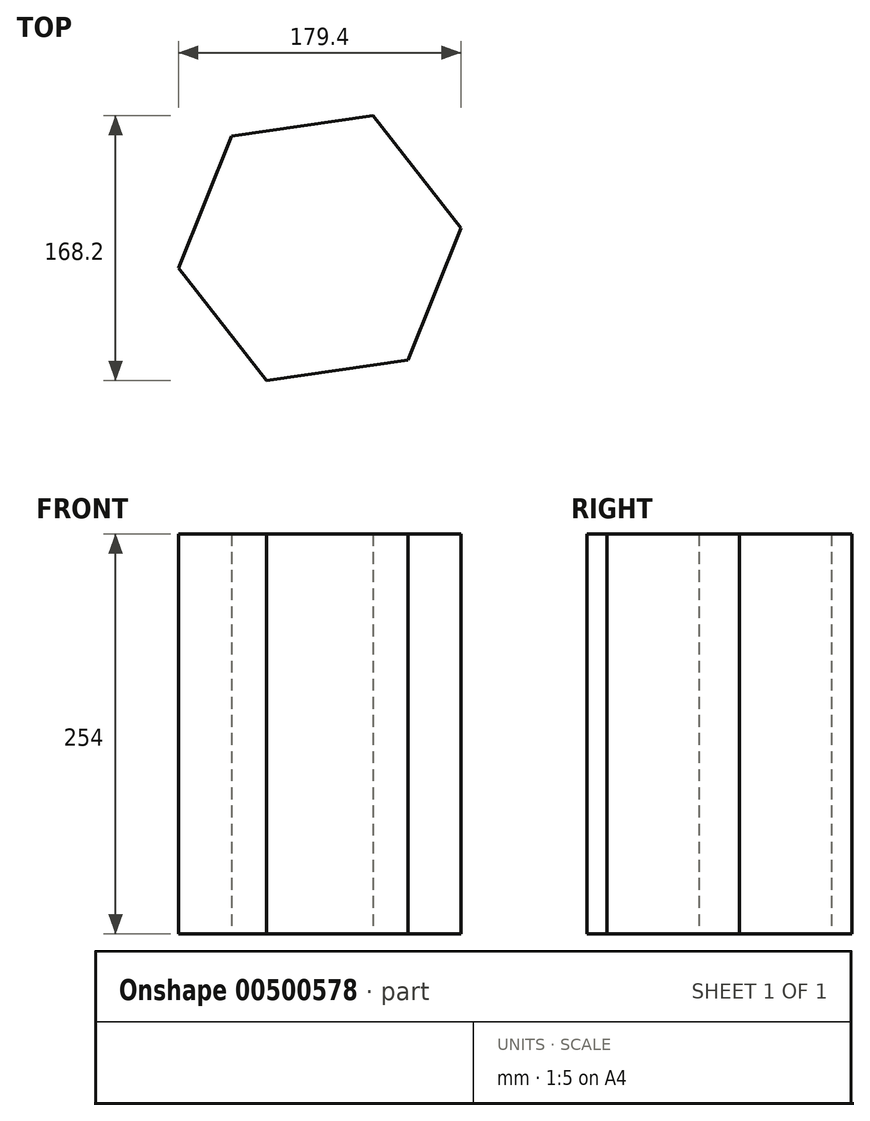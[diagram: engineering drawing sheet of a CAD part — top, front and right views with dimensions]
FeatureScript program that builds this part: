
annotation { "Feature Type Name" : "Feature", "Feature Type Description" : "" }
export const myFeature = defineFeature(function(context is Context, id is Id, definition is map)
    precondition{}
    {
        {
            var Q0;
            Q0=qCreatedBy(makeId("Top.planeOp"),FACE);
            var sketch = newSketch(context, id + "F0", { "sketchPlane" : qUnion([Q0])});
            skPoint(sketch, "E0", {"position": v(-9.33, 0) * mm});
            skCircle(sketch, "E1.cCircle", {"center": v(-9.33, 0) * mm, "radius": 90.61 * mm, "construction": true});
            skLineSegment(sketch, "E1.0", {"start": v(-65.3, 71.27) * mm, "end": v(24.4, 84.1) * mm});
            skLineSegment(sketch, "E1.1", {"start": v(24.4, 84.1) * mm, "end": v(80.37, 12.83) * mm});
            skLineSegment(sketch, "E1.2", {"start": v(80.37, 12.83) * mm, "end": v(46.64, -71.27) * mm});
            skLineSegment(sketch, "E1.3", {"start": v(46.64, -71.27) * mm, "end": v(-43.06, -84.1) * mm});
            skLineSegment(sketch, "E1.4", {"start": v(-43.06, -84.1) * mm, "end": v(-99.03, -12.83) * mm});
            skLineSegment(sketch, "E1.5", {"start": v(-99.03, -12.83) * mm, "end": v(-65.3, 71.27) * mm});
            skSolve(sketch);
        }
        {
            var Q0;
            Q0 = qSketchRegion(id + "F0", true);
            extrude(context, id + "F1", {"entities" : qUnion([Q0]), "depth" : 254 * mm});
        }
    });
